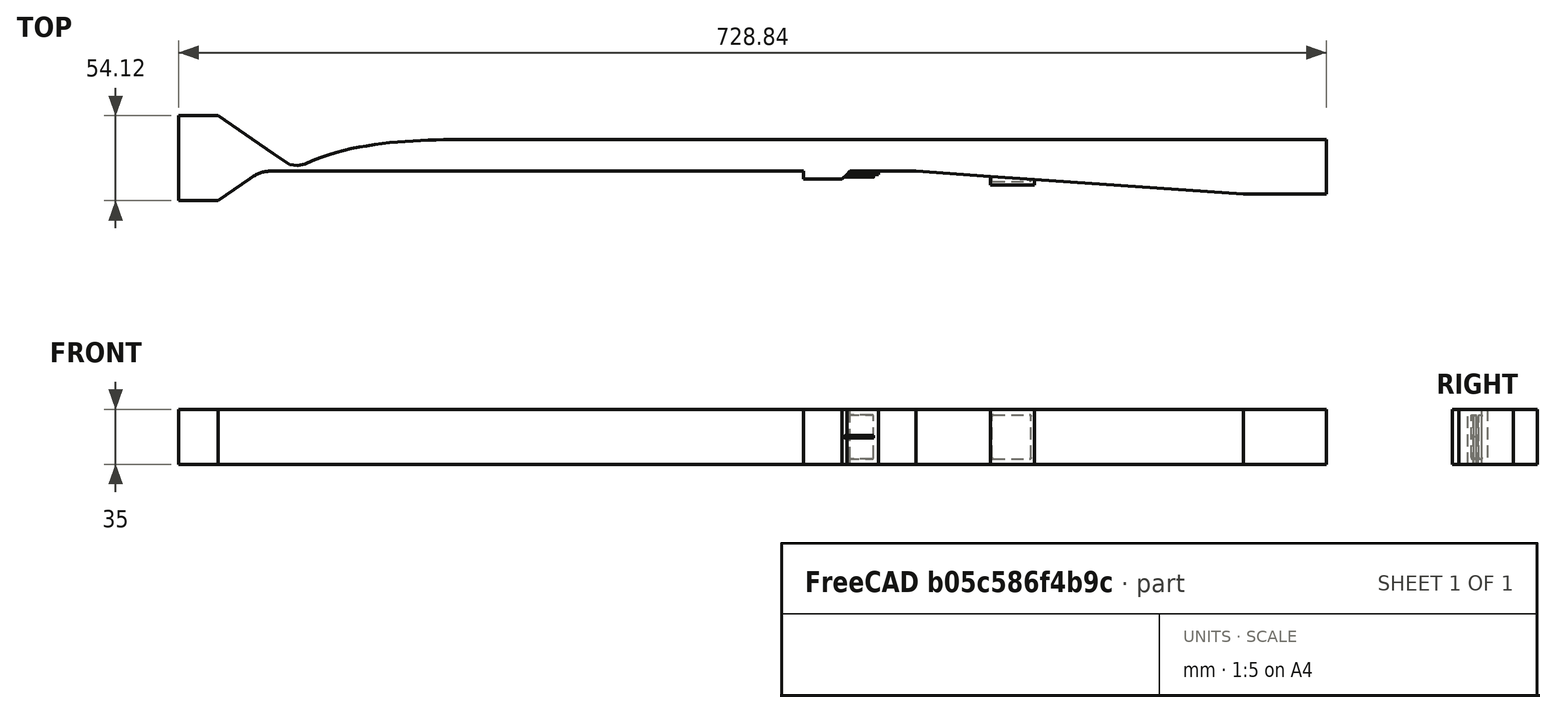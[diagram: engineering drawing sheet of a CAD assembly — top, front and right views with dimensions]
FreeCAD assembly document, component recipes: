
FREECAD ASSEMBLY — COMPONENT RECIPES ("actii-round2")

This assembly document has 6 components, labeled P0..P5 below (a component is one placed body or linked part). 4 of them carry a construction recipe — the FreeCAD feature program that regenerates the part from scratch, quoted from this document or its linked companion documents; the rest are supplied as boundary geometry only. No exploded tour is included for this assembly.
COMPONENT P0 — recipe-attached ("Fluid001", modeled in this document).
Construction recipe (the document's own serialized feature program — sketch geometry with constraints, then the solid features built on it; lengths are millimeters unless a unit is written):

FEATURE [Sketcher::SketchObject] Sketch002  label="Fluid2DProfile001"
  FullyConstrained = true
  MapMode = 5
  Support = -> [XY_Plane001]
  sketch-geometry (16):
    g0: LineSegment StartX=209.437 StartY=27.0645 StartZ=0 EndX=234.437 EndY=27.0645 EndZ=0
    g1: BSplineCurve PolesCount=155 KnotsCount=153 Degree=3 IsPeriodic=0
    g2: LineSegment StartX=209.437 StartY=-27.0645 StartZ=0 EndX=234.437 EndY=-27.0645 EndZ=0
    g3: BSplineCurve PolesCount=28 KnotsCount=26 Degree=3 IsPeriodic=0
    g4: LineSegment StartX=383.28 StartY=11.6755 StartZ=0 EndX=938.28 EndY=11.6755 EndZ=0
    g5: LineSegment StartX=606.28 StartY=-8.32451 StartZ=0 EndX=606.28 EndY=-13.3245 EndZ=0
    g6: LineSegment StartX=606.28 StartY=-13.3245 StartZ=0 EndX=630.78 EndY=-13.3245 EndZ=0
    g7: LineSegment StartX=630.78 StartY=-13.3245 StartZ=0 EndX=635.78 EndY=-8.32451 EndZ=0
    g8: LineSegment StartX=635.78 StartY=-8.32451 StartZ=0 EndX=677.78 EndY=-8.32451 EndZ=0
    g9: LineSegment StartX=677.78 StartY=-8.32451 StartZ=0 EndX=885.78 EndY=-22.8693 EndZ=0
    g10: LineSegment StartX=938.28 StartY=11.6755 StartZ=0 EndX=938.28 EndY=-22.8693 EndZ=0
    g11: LineSegment StartX=885.78 StartY=-22.8693 StartZ=0 EndX=938.28 EndY=-22.8693 EndZ=0
    g12: LineSegment StartX=274.611 StartY=-8.32451 StartZ=0 EndX=606.28 EndY=-8.32451 EndZ=0
    g13: LineSegment StartX=269.437 StartY=2.95465 StartZ=0 EndX=234.437 EndY=27.0645 EndZ=0
    g14: LineSegment StartX=209.437 StartY=27.0645 StartZ=0 EndX=209.437 EndY=-27.0645 EndZ=0
    g15: LineSegment StartX=234.437 StartY=-27.0645 StartZ=0 EndX=254.652 EndY=-13.0512 EndZ=0
  constraints (44):
    c: Block(g1)
    c: Block(g3)
    c: DistanceX(g1,g4) = 555  'iso+cav+comb'
    c: Coincident(g4,g10)
    c: Vertical(g10)
    c: Coincident(g11,g10)
    c: Horizontal(g11)
    c: Coincident(g9,g8)
    c: Horizontal(g8)
    c: Horizontal(g6)
    c: Vertical(g5)
    c: Coincident(g11,g9)
    c: DistanceY(g5,g1) = 20
    c: Coincident(g8,g7)
    c: Horizontal(g4)
    c: DistanceX(g1,g5) = 223
    c: Coincident(g5,g6)
    c: DistanceX(g5,g6) = 24.5
    c: Coincident(g6,g7)
    c: DistanceX(g6,g7) = 5
    c: DistanceX(g5,g8) = 71.5
    c: Angle(g9,g4) = 0.0698132
    c: DistanceY(g5,g5) = 5
    c: DistanceY(g6,g7) = 5
    c: Coincident(g4,g1)
    c: DistanceX(g8,g9) = 208
    c: DistanceX(g0,g1) = 35
    c: DistanceX(g0,g0) = 25
    c: DistanceX(g2,g2) = 25
    c: Coincident(g12,g3)
    c: Coincident(g12,g5)
    c: Horizontal(g12)
    c: Coincident(g13,g1)
    c: Coincident(g13,g0)
    c: Coincident(g14,g0)
    c: Coincident(g14,g2)
    c: Vertical(g14)
    c: Coincident(g15,g2)
    c: Coincident(g15,g3)
    c: DistanceX(g2,g3) = 20.2152
    c: DistanceY(g2,g3) = 14.0133
    c: DistanceY(g1,g0) = 24.1099
    c: Horizontal(g0)
    c: Horizontal(g2)
FEATURE [PartDesign::Pad] Pad003
  AllowMultiFace = false
  Direction = (0,0,1)
  Length = 35
  Length2 = 100
  Midplane = true
  Profile = -> Sketch002
  Type = 0
FEATURE [PartDesign::Body] Body001  label="Fluid"
  Group = -> [Sketch002,Pad003]
  Origin = -> Origin001
  Tip = -> Pad003
COMPONENT P1 — same part as P0; its construction recipe is shown at P0.
COMPONENT P2 — geometry summary ("wallSample001"; no construction recipe available for this part):
  bounding box: 28.0 x 16.8 x 1.8 mm
  tessellated surface: 68 triangles
  volume: 801 mm^3 (95% of its bounding box)
  symmetry: mirror-symmetric across its z mid-plane
COMPONENT P3 — same part as P0; its construction recipe is shown at P0.
COMPONENT P4 — same part as P0; its construction recipe is shown at P0.
COMPONENT P5 — geometry summary ("WallSampleComb001"; no construction recipe available for this part):
  bounding box: 28.0 x 25.0 x 3.3 mm
  tessellated surface: 100 triangles
  volume: 1709 mm^3 (74% of its bounding box)
  symmetry: mirror-symmetric across its z mid-plane
PROVENANCE & LICENSES
A FreeCAD (.FCStd) document from a public repository crawl; recipes are the document's own serialized feature recipes (and, for linked parts, companion documents' recipes).
License: as declared in the source repository (recorded in the dataset sidecar).
